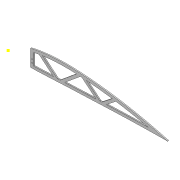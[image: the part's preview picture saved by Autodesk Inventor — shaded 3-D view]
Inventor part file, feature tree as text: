
AUTODESK INVENTOR PART (.ipt)
format: ipt  version: 2022 (Build 260153000, 153)  size: 324,608 bytes
history: native  units: mm
features: sketch x8, extrude x7, projected_geometry x4, shell x1
ambient origin geometry x8: Origin, YZ Plane, XZ Plane, XY Plane, X Axis, Y Axis, Z Axis, Center Point
bodies: Solid1 (feature_tree)
feature tree (20):
  extrude  "Extrusion1"  Depth=5.0mm
  shell  "Shell1"  Thickness=6.0mm
  extrude  "Extrusion2"  Depth=2.0mm
  extrude  "Extrusion3"  Depth=5.9mm
  extrude  "Extrusion4"  Depth=10.0mm TaperAngle=0.0deg
  extrude  "Extrusion5"  Depth=10.0mm TaperAngle=0.0deg
  extrude  "Extrusion7"  Depth=5.0mm
  sketch  "Sketch15"  dims[d20=5.0mm d21=5.0mm]
  sketch  "Sketch16"  dims[d22=4.5mm d23=0.0mm d24=2.0mm d26=2.0mm d29=4.5mm d30=0.0mm d31=2.5mm d32=0.0mm]
  extrude  "Extrusion8"  Depth=5.0mm
  sketch  "Sketch3"  dims[d0=4.5mm d1=0.0mm d2=5.0mm d3=6.0mm]
  sketch  "Sketch7"  dims[d5=4.5mm d6=0.0mm d7=2.0mm]
  projected_geometry  "Projected Loop3"
  sketch  "Sketch8"  dims[d8=2.0mm d9=5.9mm]
  sketch  "Sketch9"  dims[d12=4.0mm d13=10.0mm d14=0.0mm]
  sketch  "Sketch10"  dims[d15=40.0mm d16=10.0mm d17=0.0mm]
  projected_geometry  "Projected Loop4"
  sketch  "Sketch14"  dims[d18=5.0mm d19=5.0mm]
  projected_geometry  "Projected Loop7"
  projected_geometry  "Projected Loop8"
